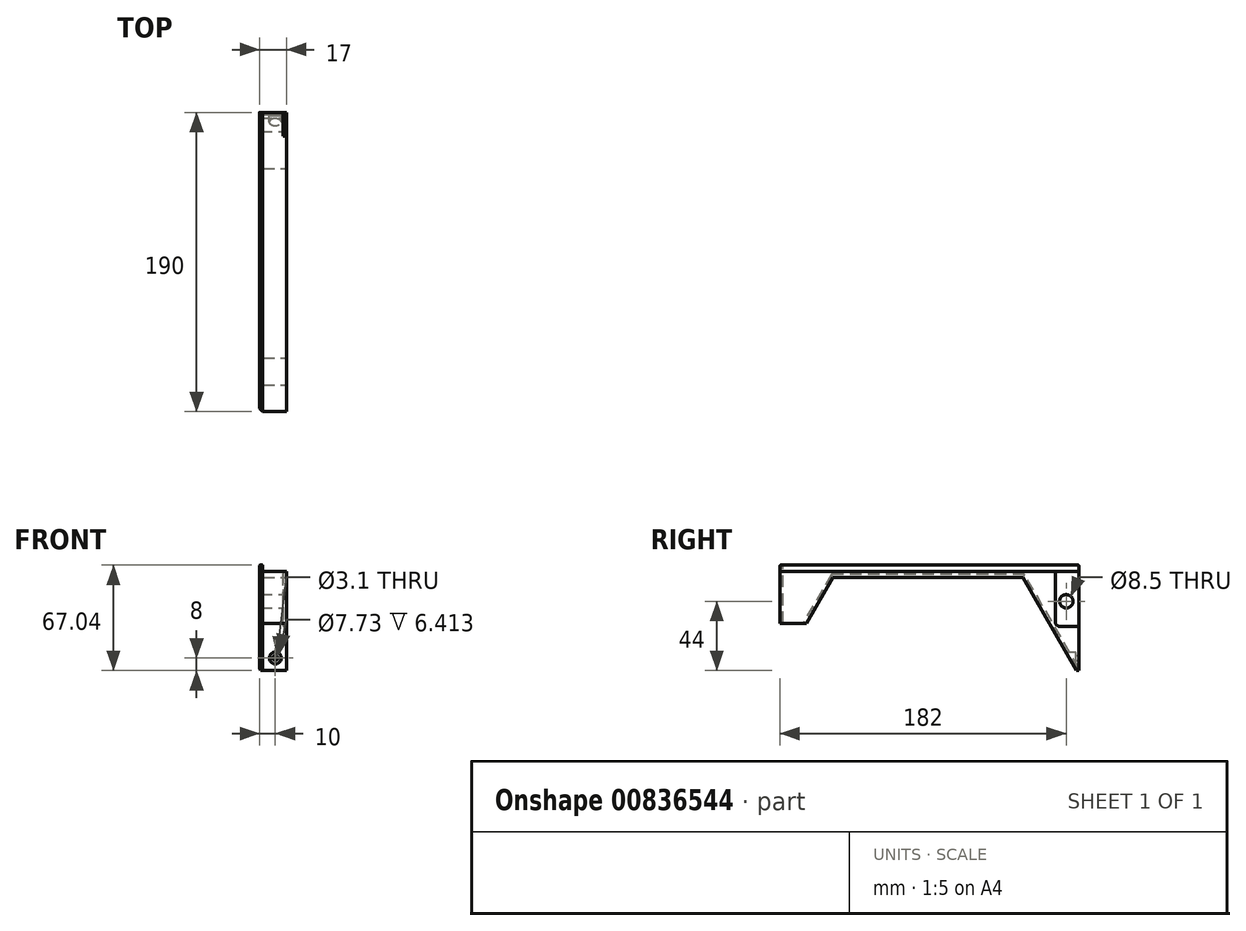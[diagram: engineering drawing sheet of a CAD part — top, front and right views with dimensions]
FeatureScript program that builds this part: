
annotation { "Feature Type Name" : "Feature", "Feature Type Description" : "" }
export const myFeature = defineFeature(function(context is Context, id is Id, definition is map)
    precondition{}
    {
        {
            var Q0;
            Q0=qCreatedBy(makeId("Front.planeOp"),FACE);
            var sketch = newSketch(context, id + "F0", { "sketchPlane" : qUnion([Q0])});
            skLineSegment(sketch, "E0", {"start": v(0, 0) * mm, "end": v(0, 63) * mm});
            skLineSegment(sketch, "E1", {"start": v(0, 63) * mm, "end": v(-17, 63) * mm});
            skLineSegment(sketch, "E2", {"start": v(-17, 63) * mm, "end": v(-17, 0) * mm});
            skLineSegment(sketch, "E3", {"start": v(-17, 0) * mm, "end": v(0, 0) * mm});
            skLineSegment(sketch, "E4", {"start": v(-2, 63) * mm, "end": v(-2, 28) * mm});
            skLineSegment(sketch, "E5", {"start": v(-2, 28) * mm, "end": v(0, 28) * mm});
            skCircle(sketch, "E6", {"center": v(-7, 8) * mm, "radius": 1.55 * mm});
            skCircle(sketch, "E7", {"center": v(-7, 8) * mm, "radius": 3.86 * mm});
            skSolve(sketch);
        }
        {
            var Q0;
            Q0=qCreatedBy(makeId("Right.planeOp"),FACE);
            var sketch = newSketch(context, id + "F1", { "sketchPlane" : qUnion([Q0])});
            skCircle(sketch, "E8", {"center": v(-8, 44) * mm, "radius": 4.25 * mm});
            skLineSegment(sketch, "E9", {"start": v(0, 0) * mm, "end": v(-1.51, 0) * mm});
            skLineSegment(sketch, "E10", {"start": v(-1.51, 0) * mm, "end": v(-38, 63) * mm});
            skLineSegment(sketch, "E11", {"start": v(-38, 63) * mm, "end": v(0, 63) * mm});
            skLineSegment(sketch, "E12", {"start": v(0, 63) * mm, "end": v(0, 0) * mm});
            skLineSegment(sketch, "E13", {"start": v(-38, 63) * mm, "end": v(-190, 63) * mm});
            skLineSegment(sketch, "E14", {"start": v(-190, 63) * mm, "end": v(-190, 59) * mm});
            skLineSegment(sketch, "E15", {"start": v(-190, 59) * mm, "end": v(-35.68, 59) * mm});
            skLineSegment(sketch, "E16", {"start": v(-35.68, 59) * mm, "end": v(0, 59) * mm});
            skLineSegment(sketch, "E17", {"start": v(0, 63) * mm, "end": v(0, 67.04) * mm});
            skLineSegment(sketch, "E18", {"start": v(0, 67.04) * mm, "end": v(-190, 67.04) * mm});
            skLineSegment(sketch, "E19", {"start": v(-190, 67.04) * mm, "end": v(-190, 63) * mm});
            skLineSegment(sketch, "E20", {"start": v(0, 28) * mm, "end": v(-15, 28) * mm});
            skLineSegment(sketch, "E21", {"start": v(-15, 28) * mm, "end": v(-15, 67.04) * mm});
            skLineSegment(sketch, "E22", {"start": v(0, 55.41) * mm, "end": v(-33.6, 55.41) * mm});
            skLineSegment(sketch, "E23", {"start": v(-190, 59) * mm, "end": v(-190, 30) * mm});
            skLineSegment(sketch, "E24", {"start": v(-190, 30) * mm, "end": v(-173.03, 30) * mm});
            skLineSegment(sketch, "E25", {"start": v(-173.03, 30) * mm, "end": v(-156.07, 59) * mm});
            skLineSegment(sketch, "E26", {"start": v(-190, 35.7) * mm, "end": v(-169.7, 35.7) * mm});
            skSolve(sketch);
        }
        {
            var Q0;
            {var subQ2=sQuery(id+"F1.wireOp",EDGE,"E9");Q0=makeQuery(id+"F1.imprint","IMPRINT",FACE,{"disambiguationData":[TD([[makeQuery(id+"F1.imprint","IMPRINT",EDGE,{"derivedFrom":subQ2}),-1.0]])]});}
            var Q1;
            Q1=makeQuery(id+"F1.imprint","IMPRINT",FACE,{"disambiguationData":[TD([[makeQuery(id+"F1.imprint","IMPRINT",EDGE,{"derivedFrom":sQuery(id+"F1.wireOp",EDGE,"E8")}),-1.0]])]});
            var Q2;
            {var subQ0=sQuery(id+"F1.wireOp",EDGE,"E16");var subQ1=sQuery(id+"F1.wireOp",EDGE,"E12");var subQ2=makeQuery(id+"F1.imprint","INTERSECT",VERTEX,{"derivedFrom":[subQ1,subQ0]});Q2=makeQuery(id+"F1.imprint","IMPRINT",FACE,{"disambiguationData":[TD([[makeQuery(id+"F1.imprint","IMPRINT",EDGE,{"disambiguationData":[TD([[subQ2,-1.0]])],"derivedFrom":subQ1}),-1.0]])]});}
            var Q3;
            {var subQ0=sQuery(id+"F1.wireOp",EDGE,"E16");var subQ5=sQuery(id+"F1.wireOp",EDGE,"E21");var subQ6=makeQuery(id+"F1.imprint","INTERSECT",VERTEX,{"derivedFrom":[subQ0,subQ5]});Q3=makeQuery(id+"F1.imprint","IMPRINT",FACE,{"disambiguationData":[TD([[makeQuery(id+"F1.imprint","IMPRINT",EDGE,{"disambiguationData":[TD([[subQ6,1.0]])],"derivedFrom":subQ5}),1.0]])]});}
            var Q4;
            {var subQ0=sQuery(id+"F1.wireOp",EDGE,"E11");var subQ5=sQuery(id+"F1.wireOp",EDGE,"E21");var subQ7=makeQuery(id+"F1.imprint","INTERSECT",VERTEX,{"derivedFrom":[subQ0,subQ5]});Q4=makeQuery(id+"F1.imprint","IMPRINT",FACE,{"disambiguationData":[TD([[makeQuery(id+"F1.imprint","IMPRINT",EDGE,{"disambiguationData":[TD([[subQ7,1.0]])],"derivedFrom":subQ5}),1.0]])]});}
            var Q5;
            {var subQ0=sQuery(id+"F1.wireOp",EDGE,"E12");var subQ5=sQuery(id+"F1.wireOp",EDGE,"E16");var subQ6=makeQuery(id+"F1.imprint","INTERSECT",VERTEX,{"derivedFrom":[subQ0,subQ5]});Q5=makeQuery(id+"F1.imprint","IMPRINT",FACE,{"disambiguationData":[TD([[makeQuery(id+"F1.imprint","IMPRINT",EDGE,{"disambiguationData":[TD([[subQ6,1.0]])],"derivedFrom":subQ5}),1.0]])]});}
            var Q6;
            {var subQ0=sQuery(id+"F1.wireOp",EDGE,"E13");Q6=makeQuery(id+"F1.imprint","IMPRINT",FACE,{"disambiguationData":[TD([[makeQuery(id+"F1.imprint","IMPRINT",EDGE,{"derivedFrom":subQ0}),1.0]])]});}
            var Q7;
            {var subQ5=sQuery(id+"F1.wireOp",EDGE,"E26");Q7=makeQuery(id+"F1.imprint","IMPRINT",FACE,{"disambiguationData":[TD([[makeQuery(id+"F1.imprint","IMPRINT",EDGE,{"derivedFrom":subQ5}),1.0]])]});}
            var Q8;
            {var subQ0=sQuery(id+"F1.wireOp",EDGE,"E24");Q8=makeQuery(id+"F1.imprint","IMPRINT",FACE,{"disambiguationData":[TD([[makeQuery(id+"F1.imprint","IMPRINT",EDGE,{"derivedFrom":subQ0}),1.0]])]});}
            extrude(context, id + "F2", {"entities" : qUnion([Q0, Q1, Q2, Q3, Q4, Q5, Q6, Q7, Q8]), "oppositeDirection" : true, "depth" : 17 * mm, "offsetDistance" : 25 * mm});
        }
        {
            var Q0;
            Q0=makeQuery(id+"F1.imprint","IMPRINT",FACE,{"disambiguationData":[TD([[makeQuery(id+"F1.imprint","IMPRINT",EDGE,{"derivedFrom":sQuery(id+"F1.wireOp",EDGE,"E8")}),-1.0]])]});
            var Q1;
            {var subQ0=sQuery(id+"F1.wireOp",EDGE,"E16");var subQ1=sQuery(id+"F1.wireOp",EDGE,"E12");var subQ2=makeQuery(id+"F1.imprint","INTERSECT",VERTEX,{"derivedFrom":[subQ1,subQ0]});Q1=makeQuery(id+"F1.imprint","IMPRINT",FACE,{"disambiguationData":[TD([[makeQuery(id+"F1.imprint","IMPRINT",EDGE,{"disambiguationData":[TD([[subQ2,-1.0]])],"derivedFrom":subQ1}),-1.0]])]});}
            var Q2;
            {var subQ0=sQuery(id+"F1.wireOp",EDGE,"E12");var subQ5=sQuery(id+"F1.wireOp",EDGE,"E16");var subQ6=makeQuery(id+"F1.imprint","INTERSECT",VERTEX,{"derivedFrom":[subQ0,subQ5]});Q2=makeQuery(id+"F1.imprint","IMPRINT",FACE,{"disambiguationData":[TD([[makeQuery(id+"F1.imprint","IMPRINT",EDGE,{"disambiguationData":[TD([[subQ6,1.0]])],"derivedFrom":subQ5}),1.0]])]});}
            extrude(context, id + "F3", {"entities" : qUnion([Q0, Q1, Q2]), "operationType" : NewBodyOperationType.REMOVE, "oppositeDirection" : true, "depth" : 2 * mm, "offsetDistance" : 25 * mm});
        }
        {
            var Q0;
            {var subQ4=sQuery(id+"F1.wireOp",EDGE,"E13");Q0=makeQuery(id+"F1.imprint","IMPRINT",FACE,{"disambiguationData":[TD([[makeQuery(id+"F1.imprint","IMPRINT",EDGE,{"derivedFrom":subQ4}),-1.0]])]});}
            var Q1;
            {var subQ0=sQuery(id+"F1.wireOp",EDGE,"E17");Q1=makeQuery(id+"F1.imprint","IMPRINT",FACE,{"disambiguationData":[TD([[makeQuery(id+"F1.imprint","IMPRINT",EDGE,{"derivedFrom":subQ0}),1.0]])]});}
            extrude(context, id + "F4", {"entities" : qUnion([Q0, Q1]), "operationType" : NewBodyOperationType.ADD, "oppositeDirection" : true, "depth" : 17 * mm, "offsetDistance" : 25 * mm, "hasSecondDirection" : true, "secondDirectionOppositeDirection" : true, "secondDirectionDepth" : 15 * mm});
        }
        {
            var Q0;
            Q0=makeQuery(id+"F3.boolean.opBoolean","COPY",EDGE,{"derivedFrom":makeQuery(id+"F3.opExtrude","SWEPT_EDGE",EDGE,{"disambiguationData":[OSD([sQuery(id+"F1.wireOp",EDGE,"E20"),sQuery(id+"F1.wireOp",EDGE,"E21")])]})});
            var Q1;
            Q1=makeQuery(id+"F3.boolean.opBoolean","COPY",EDGE,{"derivedFrom":makeQuery(id+"F3.opExtrude","SWEPT_EDGE",EDGE,{"disambiguationData":[OSD([sQuery(id+"F1.wireOp",EDGE,"E11"),sQuery(id+"F1.wireOp",EDGE,"E21")])]})});
            var Q2;
            Q2=makeQuery(id+"F3.boolean.opBoolean","COPY",EDGE,{"derivedFrom":makeQuery(id+"F3.opExtrude","SWEPT_EDGE",EDGE,{"disambiguationData":[OSD([sQuery(id+"F1.wireOp",EDGE,"E12"),sQuery(id+"F1.wireOp",EDGE,"E20")])]})});
            fillet(context, id + "F5", {"entities" : qUnion([Q0, Q1, Q2]), "radius" : 3 * mm, "tangentPropagation" : true, "allowEdgeOverflow" : false});
        }
        {
            var Q0;
            Q0=makeQuery(id+"F0.imprint","IMPRINT",FACE,{"disambiguationData":[TD([[makeQuery(id+"F0.imprint","IMPRINT",EDGE,{"derivedFrom":sQuery(id+"F0.wireOp",EDGE,"E6")}),1.0]])]});
            extrude(context, id + "F6", {"entities" : qUnion([Q0]), "operationType" : NewBodyOperationType.REMOVE, "depth" : 25 * mm, "offsetDistance" : 25 * mm});
        }
        {
            var Q0;
            Q0=makeQuery(id+"F0.imprint","IMPRINT",FACE,{"disambiguationData":[TD([[makeQuery(id+"F0.imprint","IMPRINT",EDGE,{"derivedFrom":sQuery(id+"F0.wireOp",EDGE,"E6")}),-1.0]])]});
            extrude(context, id + "F7", {"entities" : qUnion([Q0]), "operationType" : NewBodyOperationType.REMOVE, "depth" : 25 * mm, "offsetDistance" : 25 * mm, "hasSecondDirection" : true, "secondDirectionOppositeDirection" : false, "secondDirectionDepth" : 2 * mm});
        }
        {
            var Q0;
            Q0=makeQuery(id+"F2.opExtrude","CAP_EDGE",EDGE,{"disambiguationData":[OSD([sQuery(id+"F1.wireOp",EDGE,"E10")])],"isStart":false});
            var Q1;
            Q1=makeQuery(id+"F2.opExtrude","CAP_EDGE",EDGE,{"disambiguationData":[OSD([sQuery(id+"F1.wireOp",EDGE,"E15")])],"isStart":false});
            var Q2;
            Q2=makeQuery(id+"F2.opExtrude","CAP_EDGE",EDGE,{"disambiguationData":[OSD([sQuery(id+"F1.wireOp",EDGE,"E25")])],"isStart":false});
            var Q3;
            Q3=makeQuery(id+"F2.opExtrude","CAP_EDGE",EDGE,{"disambiguationData":[OSD([sQuery(id+"F1.wireOp",EDGE,"E14"),sQuery(id+"F1.wireOp",EDGE,"E23")])],"isStart":false});
            chamfer(context, id + "F8", {"entities" : qUnion([Q0, Q1, Q2, Q3]), "width" : 2 * mm, "tangentPropagation" : true});
        }
        {
            var Q0;
            Q0=makeQuery(id+"F4.opExtrude","CAP_EDGE",EDGE,{"disambiguationData":[OSD([sQuery(id+"F1.wireOp",EDGE,"E11"),sQuery(id+"F1.wireOp",EDGE,"E13")])],"isStart":true});
            var Q1;
            Q1=makeQuery(id+"F4.opExtrude","CAP_EDGE",EDGE,{"disambiguationData":[OSD([sQuery(id+"F1.wireOp",EDGE,"E18")])],"isStart":true});
            var Q2;
            Q2=makeQuery(id+"F4.opExtrude","CAP_EDGE",EDGE,{"disambiguationData":[OSD([sQuery(id+"F1.wireOp",EDGE,"E18")])],"isStart":false});
            var Q3;
            Q3=makeQuery(id+"F8.opChamfer","BLEND_EDGE",EDGE,{"blendedFrom":[makeQuery(id+"F4.boolean.opBoolean","MERGE",EDGE,{"derivedFrom":[makeQuery(id+"F2.opExtrude","CAP_EDGE",EDGE,{"disambiguationData":[OSD([sQuery(id+"F1.wireOp",EDGE,"E14"),sQuery(id+"F1.wireOp",EDGE,"E23")])],"isStart":false}),makeQuery(id+"F4.opExtrude","CAP_EDGE",EDGE,{"disambiguationData":[OSD([sQuery(id+"F1.wireOp",EDGE,"E19")])],"isStart":false})]}),makeQuery(id+"F4.opExtrude","SWEPT_FACE",FACE,{"disambiguationData":[OSD([sQuery(id+"F1.wireOp",EDGE,"E18")])]})],"blendedInto":[makeQuery(id+"F4.opExtrude","SWEPT_FACE",FACE,{"disambiguationData":[OSD([sQuery(id+"F1.wireOp",EDGE,"E18")])]})]});
            var Q4;
            Q4=makeQuery(id+"F4.opExtrude","SWEPT_EDGE",EDGE,{"disambiguationData":[OSD([sQuery(id+"F1.wireOp",EDGE,"E17"),sQuery(id+"F1.wireOp",EDGE,"E18")])]});
            var Q5;
            Q5=makeQuery(id+"F2.opExtrude","CAP_EDGE",EDGE,{"disambiguationData":[OSD([sQuery(id+"F1.wireOp",EDGE,"E8")])],"isStart":false});
            fillet(context, id + "F9", {"entities" : qUnion([Q0, Q1, Q2, Q3, Q4, Q5]), "radius" : 0.5 * mm, "tangentPropagation" : true, "allowEdgeOverflow" : false});
        }
    });
